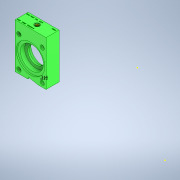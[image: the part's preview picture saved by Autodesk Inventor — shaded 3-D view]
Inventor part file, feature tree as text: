
AUTODESK INVENTOR PART (.ipt)
format: ipt  version: 2020 (Build 240168000, 168)  size: 569,344 bytes
history: native  units: in
note: dims shown in document units (in); Inventor stores cm internally (conversion verified against a paired STEP export)
features: hole x6, sketch x5, extrude x4, fillet x1
ambient origin geometry x8: Origin, YZ Plane, XZ Plane, XY Plane, X Axis, Y Axis, Z Axis, Center Point
bodies: Solid1 (feature_tree)
feature tree (16):
  extrude  "Extrusion1"  Depth=0.4in TaperAngle=0.0deg
  extrude  "Extrusion2"  Depth=0.25in
  sketch  "Sketch3"  dims[d6=0.213in d7=0.75in d8=0.507in d9=0.25in d10=0.5635in d11=0.25in d12=0.0in]
  extrude  "Extrusion3"  Depth=0.0312in
  hole  "Hole1"  [1 undecoded]
  hole  "Hole2"  [1 undecoded]
  extrude  "Extrusion4"  Depth=0.0312in
  hole  "Hole5"  [1 undecoded]
  hole  "Hole6"  [1 undecoded]
  fillet  "Fillet1"  Radius=0.314in
  sketch  "Sketch4"  dims[d13=0.04in d14=0.75in d15=0.507in d16=0.25in d17=0.5635in d18=1.0in d19=0.8108in d20=0.4583in]
  hole  "Hole3"  [1 undecoded]
  hole  "Hole4"  [1 undecoded]
  sketch  "Sketch1"  dims[d0=0.4in d1=0.0in d2=0.4in d3=0.0in]
  sketch  "Sketch2"  dims[d4=0.6in d5=0.0in]
  sketch  "Sketch5"  dims[d21=0.29in d22=0.04in d23=0.75in d24=0.507in d25=0.25in d26=0.5635in d27=1.0in d28=0.8108in d29=0.213in d30=0.75in d31=0.507in d32=0.25in d33=0.5635in d34=0.25in d35=0.0in d36=0.75in d38=135.0deg d39=0.4583in d40=0.6957in d41=0.25in d42=1.0in d43=0.0in d44=0.314in d45=0.221in d46=0.213in d47=0.75in d48=0.375in d49=0.25in d50=0.5635in d51=0.25in d52=0.0in d53=0.06in d54=0.75in d55=0.375in d56=0.25in d57=0.5635in d58=0.6in d59=0.8108in d60=0.0312in d61=1.1595in d62=0.221in]
note: 6 required parameter values undecoded (feature->parameter linkage not recoverable at this tier; creation-order binding heuristic only, values carry confidence <= 0.55)
